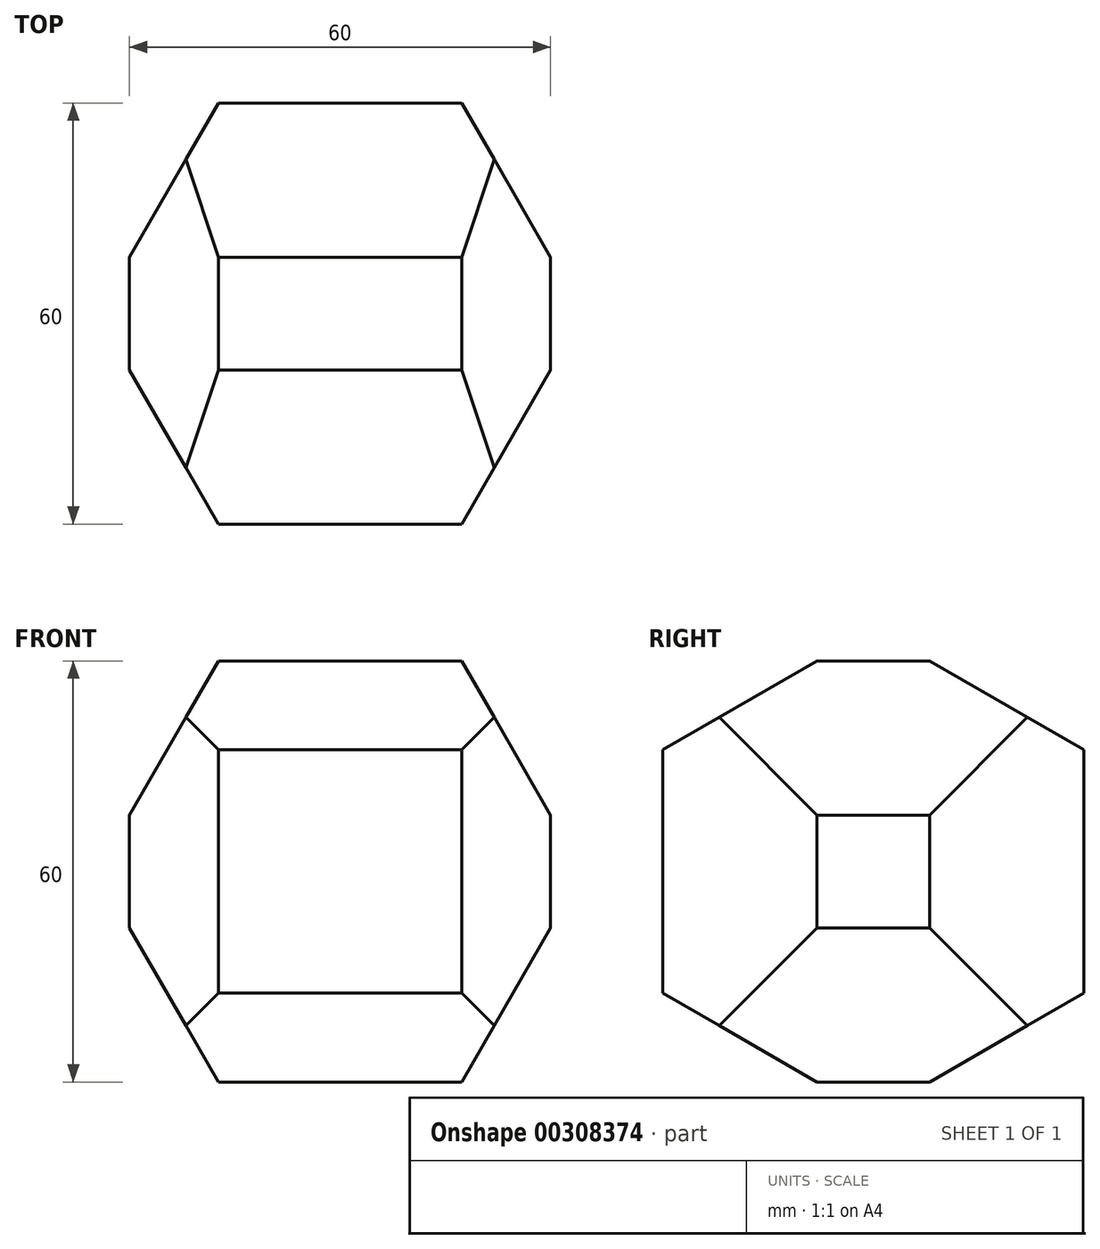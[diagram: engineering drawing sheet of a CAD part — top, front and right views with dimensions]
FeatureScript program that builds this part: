
annotation { "Feature Type Name" : "Feature", "Feature Type Description" : "" }
export const myFeature = defineFeature(function(context is Context, id is Id, definition is map)
    precondition{}
    {
        {
            var Q0;
            Q0=qCreatedBy(makeId("Top.planeOp"),FACE);
            var sketch = newSketch(context, id + "F0", { "sketchPlane" : qUnion([Q0])});
            skCircle(sketch, "E0.cCircle", {"center": v(0, 0) * mm, "radius": 30 * mm, "construction": true});
            skLineSegment(sketch, "E0.0", {"start": v(-17.32, 30) * mm, "end": v(17.32, 30) * mm});
            skLineSegment(sketch, "E0.1", {"start": v(17.32, 30) * mm, "end": v(34.64, 0) * mm});
            skLineSegment(sketch, "E0.2", {"start": v(34.64, 0) * mm, "end": v(17.32, -30) * mm});
            skLineSegment(sketch, "E0.3", {"start": v(17.32, -30) * mm, "end": v(-17.32, -30) * mm});
            skLineSegment(sketch, "E0.4", {"start": v(-17.32, -30) * mm, "end": v(-34.64, 0) * mm});
            skLineSegment(sketch, "E0.5", {"start": v(-34.64, 0) * mm, "end": v(-17.32, 30) * mm});
            skPoint(sketch, "E0.0.midPoint", {"position": v(0, 30) * mm});
            skSolve(sketch);
        }
        {
            var Q0;
            Q0=qCreatedBy(makeId("Right.planeOp"),FACE);
            var sketch = newSketch(context, id + "F1", { "sketchPlane" : qUnion([Q0])});
            skCircle(sketch, "E1.cCircle", {"center": v(0, 0) * mm, "radius": 30 * mm, "construction": true});
            skLineSegment(sketch, "E1.0", {"start": v(30, 17.32) * mm, "end": v(30, -17.32) * mm});
            skLineSegment(sketch, "E1.1", {"start": v(30, -17.32) * mm, "end": v(0, -34.64) * mm});
            skLineSegment(sketch, "E1.2", {"start": v(0, -34.64) * mm, "end": v(-30, -17.32) * mm});
            skLineSegment(sketch, "E1.3", {"start": v(-30, -17.32) * mm, "end": v(-30, 17.32) * mm});
            skLineSegment(sketch, "E1.4", {"start": v(-30, 17.32) * mm, "end": v(0, 34.64) * mm});
            skLineSegment(sketch, "E1.5", {"start": v(0, 34.64) * mm, "end": v(30, 17.32) * mm});
            skPoint(sketch, "E1.0.midPoint", {"position": v(30, 0) * mm});
            skSolve(sketch);
        }
        {
            var Q0;
            Q0=qCreatedBy(makeId("Front.planeOp"),FACE);
            var sketch = newSketch(context, id + "F2", { "sketchPlane" : qUnion([Q0])});
            skCircle(sketch, "E2.cCircle", {"center": v(0, 0) * mm, "radius": 30 * mm, "construction": true});
            skLineSegment(sketch, "E2.0", {"start": v(-17.32, 30) * mm, "end": v(17.32, 30) * mm});
            skLineSegment(sketch, "E2.1", {"start": v(17.32, 30) * mm, "end": v(34.64, 0) * mm});
            skLineSegment(sketch, "E2.2", {"start": v(34.64, 0) * mm, "end": v(17.32, -30) * mm});
            skLineSegment(sketch, "E2.3", {"start": v(17.32, -30) * mm, "end": v(-17.32, -30) * mm});
            skLineSegment(sketch, "E2.4", {"start": v(-17.32, -30) * mm, "end": v(-34.64, 0) * mm});
            skLineSegment(sketch, "E2.5", {"start": v(-34.64, 0) * mm, "end": v(-17.32, 30) * mm});
            skPoint(sketch, "E2.0.midPoint", {"position": v(0, 30) * mm});
            skSolve(sketch);
        }
        {
            var Q0;
            Q0 = qSketchRegion(id + "F0", true);
            extrude(context, id + "F3", {"entities" : qUnion([Q0]), "endBound" : BoundingType.SYMMETRIC, "depth" : 60 * mm});
        }
        {
            var Q0;
            Q0 = qSketchRegion(id + "F1", true);
            extrude(context, id + "F4", {"entities" : qUnion([Q0]), "operationType" : NewBodyOperationType.INTERSECT, "endBound" : BoundingType.SYMMETRIC, "depth" : 60 * mm});
        }
        {
            var Q0;
            Q0 = qSketchRegion(id + "F2", true);
            extrude(context, id + "F5", {"entities" : qUnion([Q0]), "operationType" : NewBodyOperationType.INTERSECT, "endBound" : BoundingType.SYMMETRIC, "depth" : 60 * mm});
        }
    });
